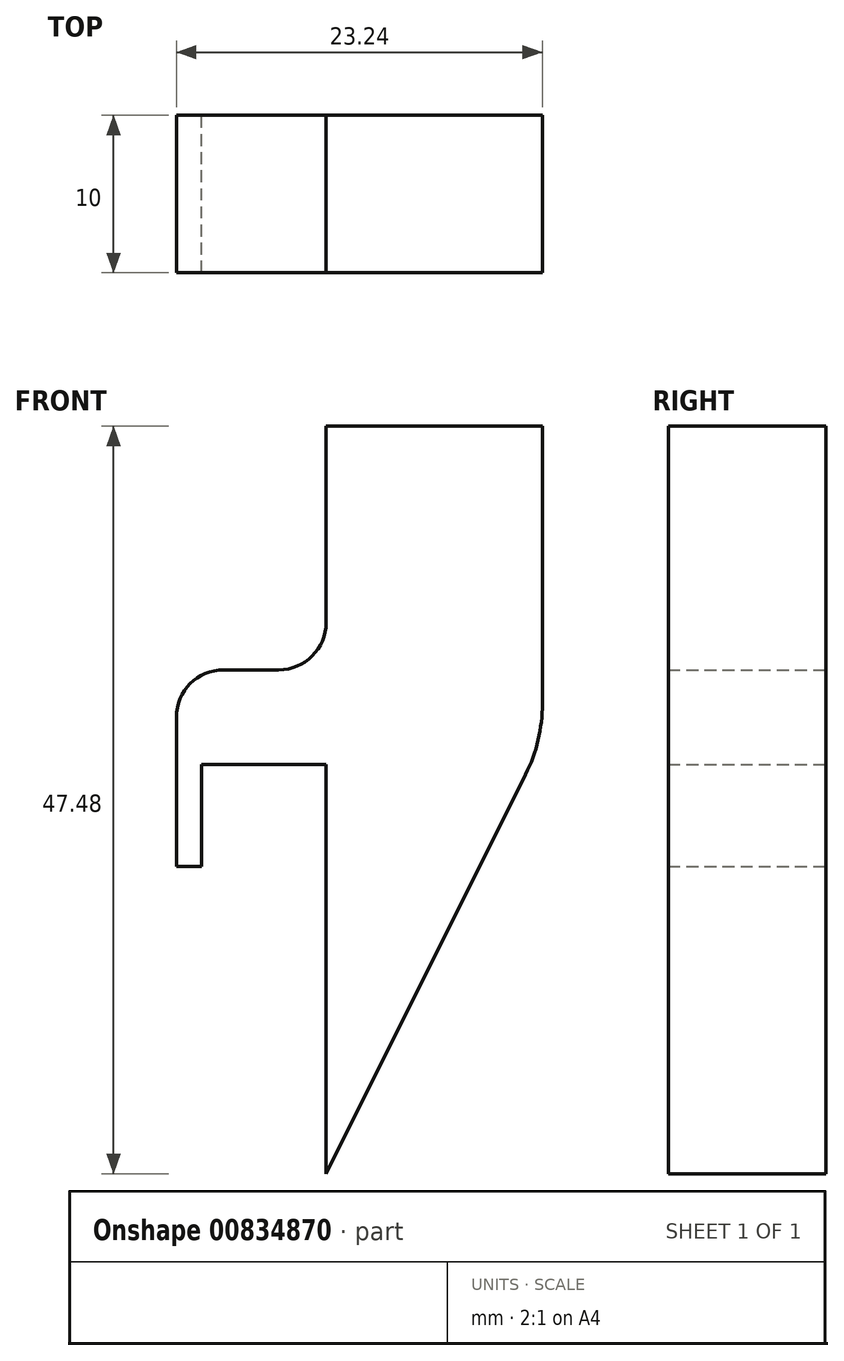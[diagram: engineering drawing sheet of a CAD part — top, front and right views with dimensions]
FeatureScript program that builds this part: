
annotation { "Feature Type Name" : "Feature", "Feature Type Description" : "" }
export const myFeature = defineFeature(function(context is Context, id is Id, definition is map)
    precondition{}
    {
        {
            var Q0;
            Q0=qCreatedBy(makeId("Front.planeOp"),FACE);
            var sketch = newSketch(context, id + "F0", { "sketchPlane" : qUnion([Q0])});
            skLineSegment(sketch, "E0.left", {"start": v(0, 9.26) * mm, "end": v(0, -16.74) * mm});
            skLineSegment(sketch, "E1", {"start": v(0, -16.74) * mm, "end": v(12.68, 8.63) * mm});
            skLineSegment(sketch, "E2.top", {"start": v(0, 30.74) * mm, "end": v(13.74, 30.74) * mm});
            skLineSegment(sketch, "E2.right", {"start": v(13.74, 13.1) * mm, "end": v(13.74, 30.74) * mm});
            skLineSegment(sketch, "E3.bottom", {"start": v(0, 9.26) * mm, "end": v(-7.9, 9.26) * mm});
            skLineSegment(sketch, "E3.top", {"start": v(-3, 15.26) * mm, "end": v(-6.5, 15.26) * mm});
            skLineSegment(sketch, "E3.right", {"start": v(-9.5, 9.26) * mm, "end": v(-9.5, 12.26) * mm});
            skLineSegment(sketch, "E4.top", {"start": v(-9.5, 2.76) * mm, "end": v(-7.9, 2.76) * mm});
            skLineSegment(sketch, "E4.left", {"start": v(-9.5, 9.26) * mm, "end": v(-9.5, 2.76) * mm});
            skLineSegment(sketch, "E4.right", {"start": v(-7.9, 9.26) * mm, "end": v(-7.9, 2.76) * mm});
            skPoint(sketch, "E5.visualSharp", {"position": v(-9.5, 15.26) * mm});
            skArc(sketch, "E5.filletArc", {"start": v(-6.5, 15.26) * mm, "mid": v(-8.62, 14.38) * mm, "end": v(-9.5, 12.26) * mm});
            skLineSegment(sketch, "E6", {"start": v(0, 18.26) * mm, "end": v(0, 30.74) * mm});
            skPoint(sketch, "E7.visualSharp", {"position": v(0, 15.26) * mm});
            skArc(sketch, "E7.filletArc", {"start": v(-3, 15.26) * mm, "mid": v(-0.88, 16.14) * mm, "end": v(0, 18.26) * mm});
            skPoint(sketch, "E8.visualSharp", {"position": v(13.74, 10.74) * mm});
            skArc(sketch, "E8.filletArc", {"start": v(12.68, 8.63) * mm, "mid": v(13.47, 10.8) * mm, "end": v(13.74, 13.1) * mm});
            skSolve(sketch);
        }
        {
            var Q0;
            Q0=makeQuery(id+"F0.imprint","IMPRINT",FACE,{"disambiguationData":[TD([[makeQuery(id+"F0.imprint","IMPRINT",EDGE,{"derivedFrom":sQuery(id+"F0.wireOp",EDGE,"E0.left")}),1.0]])]});
            extrude(context, id + "F1", {"entities" : qUnion([Q0]), "depth" : 10 * mm, "offsetDistance" : 25 * mm});
        }
    });
